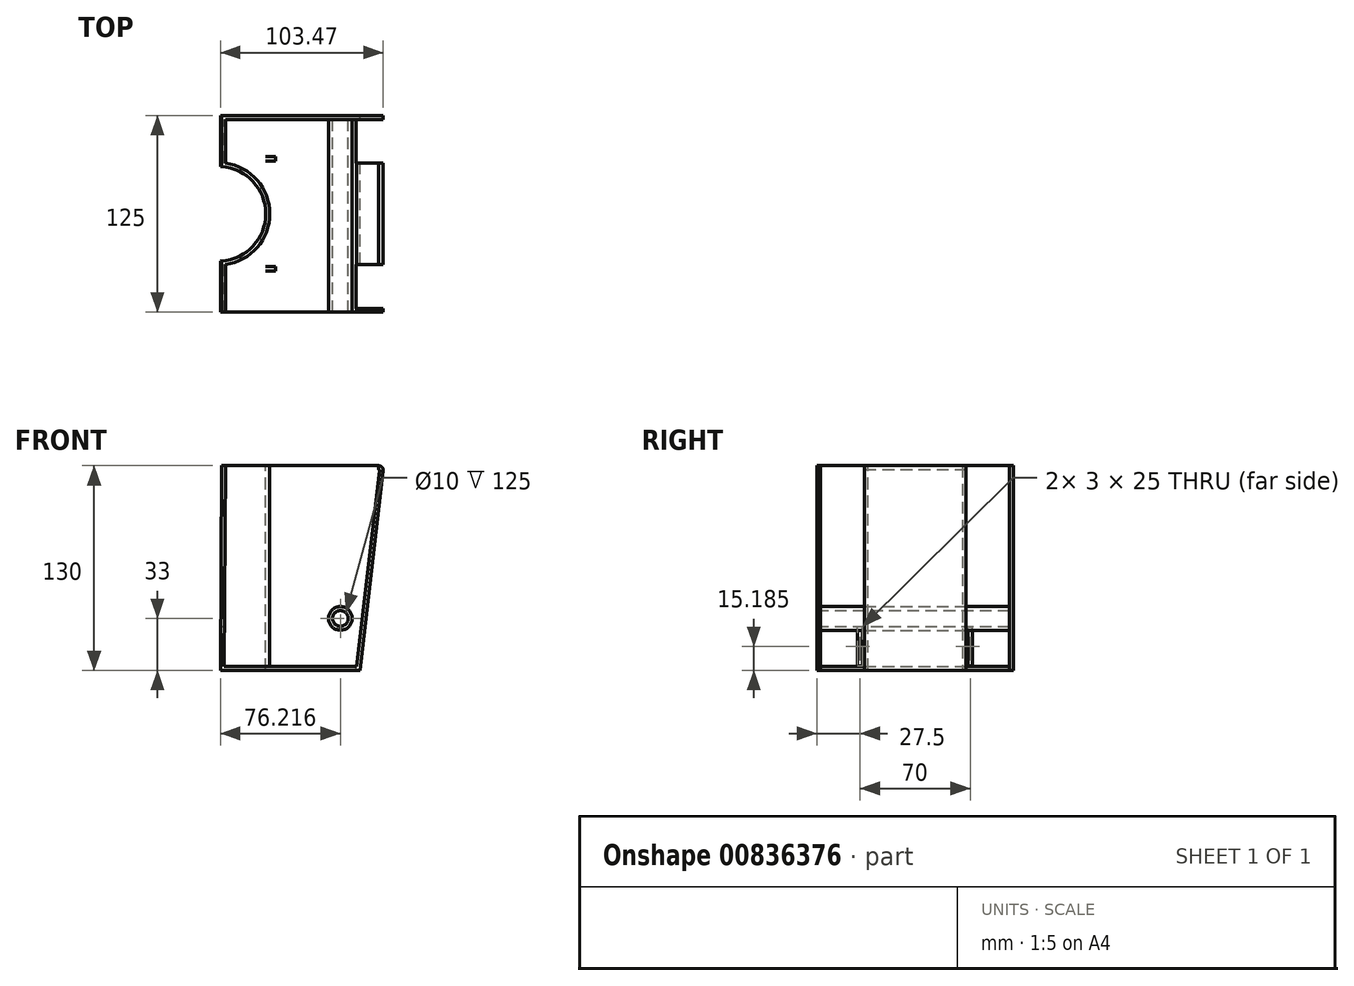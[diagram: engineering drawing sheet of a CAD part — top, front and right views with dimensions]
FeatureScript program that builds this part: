
annotation { "Feature Type Name" : "Feature", "Feature Type Description" : "" }
export const myFeature = defineFeature(function(context is Context, id is Id, definition is map)
    precondition{}
    {
        {
            var Q0;
            Q0=qCreatedBy(makeId("Front.planeOp"),FACE);
            var sketch = newSketch(context, id + "F0", { "sketchPlane" : qUnion([Q0])});
            skLineSegment(sketch, "E0", {"start": v(0, 130) * mm, "end": v(75, 130) * mm});
            skLineSegment(sketch, "E1", {"start": v(75, 130) * mm, "end": v(60, 0) * mm});
            skLineSegment(sketch, "E2", {"start": v(0, 130) * mm, "end": v(-28, 130) * mm});
            skLineSegment(sketch, "E3", {"start": v(-28.83, 0) * mm, "end": v(-28, 130) * mm});
            skLineSegment(sketch, "E4", {"start": v(75.45, 0) * mm, "end": v(-49.86, 0) * mm, "construction": true});
            skLineSegment(sketch, "E5", {"start": v(0, -37.66) * mm, "end": v(0, 158.2) * mm, "construction": true});
            skLineSegment(sketch, "E6", {"start": v(-28.83, 0) * mm, "end": v(60, 0) * mm});
            skPoint(sketch, "E7.start.orphan", {"position": v(0, -15) * mm});
            skLineSegment(sketch, "E8", {"start": v(-28.62, 33) * mm, "end": v(47.39, 33) * mm, "construction": true});
            skLineSegment(sketch, "E9", {"start": v(47.39, 0) * mm, "end": v(47.39, 50.91) * mm, "construction": true});
            skCircle(sketch, "E10", {"center": v(47.39, 33) * mm, "radius": 5 * mm});
            skSolve(sketch);
        }
        {
            var Q0;
            Q0=makeQuery(id+"F0.imprint","IMPRINT",FACE,{"disambiguationData":[TD([[makeQuery(id+"F0.imprint","IMPRINT",EDGE,{"derivedFrom":sQuery(id+"F0.wireOp",EDGE,"E0")}),-1.0]])]});
            var Q1;
            Q1=qSketchRegion(id+"F3",true);
            extrude(context, id + "F1", {"entities" : qUnion([Q0, Q1]), "depth" : 125 * mm, "offsetDistance" : 25 * mm});
        }
        {
            var Q0;
            Q0=makeQuery(id+"F1.opExtrude","SWEPT_FACE",FACE,{"disambiguationData":[OSD([sQuery(id+"F0.wireOp",EDGE,"E0"),sQuery(id+"F0.wireOp",EDGE,"E2")])]});
            cPlane(context, id + "F2", {"entities" : qUnion([Q0]), "cplaneType" : CPlaneType.OFFSET, "offset" : 0 * mm, "width" : 150 * mm, "height" : 150 * mm});
        }
        {
            var Q0;
            Q0=qCreatedBy(id+"F2.planeOp",FACE);
            var sketch = newSketch(context, id + "F3", { "sketchPlane" : qUnion([Q0])});
            skCircle(sketch, "E11", {"center": v(-30, -62.5) * mm, "radius": 30 * mm});
            skLineSegment(sketch, "E12", {"start": v(0, 0) * mm, "end": v(0, -125) * mm, "construction": true});
            skLineSegment(sketch, "E13", {"start": v(0, 0) * mm, "end": v(0, -62.5) * mm, "construction": true});
            skSolve(sketch);
        }
        {
            var Q0;
            Q0=makeQuery(id+"F3.imprint","IMPRINT",FACE,{"disambiguationData":[TD([[makeQuery(id+"F3.imprint","IMPRINT",EDGE,{"derivedFrom":sQuery(id+"F3.wireOp",EDGE,"E11")}),1.0]])]});
            extrude(context, id + "F4", {"entities" : qUnion([Q0]), "operationType" : NewBodyOperationType.REMOVE, "oppositeDirection" : true, "depth" : 171.8 * mm, "offsetDistance" : 25 * mm});
        }
        {
            var Q0;
            Q0=makeQuery(id+"F1.opExtrude","SWEPT_EDGE",EDGE,{"disambiguationData":[OSD([sQuery(id+"F0.wireOp",EDGE,"E0"),sQuery(id+"F0.wireOp",EDGE,"E1")])]});
            fillet(context, id + "F5", {"entities" : qUnion([Q0]), "radius" : 3 * mm, "tangentPropagation" : true, "allowEdgeOverflow" : false});
        }
        {
            var Q0;
            Q0=makeQuery(id+"F1.opExtrude","SWEPT_FACE",FACE,{"disambiguationData":[OSD([sQuery(id+"F0.wireOp",EDGE,"E0"),sQuery(id+"F0.wireOp",EDGE,"E2")])]});
            var Q1;
            Q1=makeQuery(id+"F1.opExtrude","CAP_FACE",FACE,{"disambiguationData":[OSD([sQuery(id+"F0.wireOp",EDGE,"E0"),sQuery(id+"F0.wireOp",EDGE,"y3vMRWIf-u3MA-5TxN-y6xK-OTS8Fqzy5Pt6"),sQuery(id+"F0.wireOp",EDGE,"xp1ytB3h-V9W0-7MQi-CCPZ-iRdVjfuMOfr9"),sQuery(id+"F0.wireOp",EDGE,"646e11d9-17b4-4f13-8456-ecb146ae1e03.trimOffspring"),sQuery(id+"F0.wireOp",EDGE,"E1"),sQuery(id+"F0.wireOp",EDGE,"E2"),sQuery(id+"F0.wireOp",EDGE,"E7"),sQuery(id+"F0.wireOp",EDGE,"E3")])],"isStart":false});
            shell(context, id + "F6", {"entities" : qUnion([Q0, Q1]), "thickness" : 2.5 * mm});
        }
        {
            var Q0;
            {var subQ0=sQuery(id+"F0.wireOp",EDGE,"E3");var subQ1=sQuery(id+"F0.wireOp",EDGE,"E7");var subQ2=sQuery(id+"F0.wireOp",EDGE,"E2");var subQ3=sQuery(id+"F0.wireOp",EDGE,"xp1ytB3h-V9W0-7MQi-CCPZ-iRdVjfuMOfr9");var subQ4=sQuery(id+"F0.wireOp",EDGE,"E0");Q0=makeQuery(id+"F4.boolean.opBoolean","SPLIT",FACE,{"disambiguationData":[TD([makeQuery(id+"F1.opExtrude","CAP_FACE",FACE,{"disambiguationData":[OSD([subQ4,sQuery(id+"F0.wireOp",EDGE,"y3vMRWIf-u3MA-5TxN-y6xK-OTS8Fqzy5Pt6"),subQ3,sQuery(id+"F0.wireOp",EDGE,"646e11d9-17b4-4f13-8456-ecb146ae1e03.trimOffspring"),sQuery(id+"F0.wireOp",EDGE,"E1"),subQ2,subQ1,subQ0])],"isStart":true})])],"derivedFrom":makeQuery(id+"F1.opExtrude","SWEPT_FACE",FACE,{"disambiguationData":[OSD([subQ0])]})});}
            cPlane(context, id + "F7", {"entities" : qUnion([Q0]), "cplaneType" : CPlaneType.OFFSET, "offset" : 0 * mm, "width" : 150 * mm, "height" : 150 * mm});
        }
        {
            var Q0;
            Q0=qCreatedBy(id+"F7.planeOp",FACE);
            var sketch = newSketch(context, id + "F8", { "sketchPlane" : qUnion([Q0])});
            skLineSegment(sketch, "E14.bottom", {"start": v(29, 2.5) * mm, "end": v(26, 2.5) * mm});
            skLineSegment(sketch, "E14.top", {"start": v(29, 27.5) * mm, "end": v(26, 27.5) * mm});
            skLineSegment(sketch, "E14.left", {"start": v(29, 2.5) * mm, "end": v(29, 27.5) * mm});
            skLineSegment(sketch, "E14.right", {"start": v(26, 2.5) * mm, "end": v(26, 27.5) * mm});
            skLineSegment(sketch, "E15.bottom", {"start": v(96, 2.5) * mm, "end": v(99, 2.5) * mm});
            skLineSegment(sketch, "E15.top", {"start": v(96, 27.5) * mm, "end": v(99, 27.5) * mm});
            skLineSegment(sketch, "E15.left", {"start": v(96, 2.5) * mm, "end": v(96, 27.5) * mm});
            skLineSegment(sketch, "E15.right", {"start": v(99, 2.5) * mm, "end": v(99, 27.5) * mm});
            skLineSegment(sketch, "E16.bottom", {"start": v(99, 2.5) * mm, "end": v(96, 2.5) * mm});
            skSolve(sketch);
        }
        {
            var Q0;
            Q0=makeQuery(id+"F8.imprint","IMPRINT",FACE,{"disambiguationData":[TD([[makeQuery(id+"F8.imprint","IMPRINT",EDGE,{"derivedFrom":sQuery(id+"F8.wireOp",EDGE,"E14.bottom")}),-1.0]])]});
            var Q1;
            Q1=makeQuery(id+"F8.imprint","IMPRINT",FACE,{"disambiguationData":[TD([[makeQuery(id+"F8.imprint","IMPRINT",EDGE,{"derivedFrom":sQuery(id+"F8.wireOp",EDGE,"E15.top")}),-1.0]])]});
            extrude(context, id + "F9", {"entities" : qUnion([Q0, Q1]), "operationType" : NewBodyOperationType.REMOVE, "oppositeDirection" : true, "depth" : 35.1 * mm, "offsetDistance" : 25 * mm});
        }
        {
            var Q0;
            Q0=qCreatedBy(id+"F7.planeOp",FACE);
            cPlane(context, id + "F10", {"entities" : qUnion([Q0]), "cplaneType" : CPlaneType.OFFSET, "offset" : 110 * mm, "oppositeDirection" : true, "width" : 150 * mm, "height" : 150 * mm});
        }
        {
            var Q0;
            Q0=qCreatedBy(id+"F10.planeOp",FACE);
            var sketch = newSketch(context, id + "F11", { "sketchPlane" : qUnion([Q0])});
            skLineSegment(sketch, "E17.bottom", {"start": v(122.5, -15) * mm, "end": v(94.75, -15) * mm});
            skLineSegment(sketch, "E17.top", {"start": v(122.5, 135) * mm, "end": v(94.75, 135) * mm});
            skLineSegment(sketch, "E17.left", {"start": v(122.5, -15) * mm, "end": v(122.5, 135) * mm});
            skLineSegment(sketch, "E17.right", {"start": v(94.75, -15) * mm, "end": v(94.75, 135) * mm});
            skLineSegment(sketch, "E18.bottom", {"start": v(30.25, -15) * mm, "end": v(2.5, -15) * mm});
            skLineSegment(sketch, "E18.top", {"start": v(30.25, 135) * mm, "end": v(2.5, 135) * mm});
            skLineSegment(sketch, "E18.left", {"start": v(30.25, -15) * mm, "end": v(30.25, 135) * mm});
            skLineSegment(sketch, "E18.right", {"start": v(2.5, -15) * mm, "end": v(2.5, 135) * mm});
            skSolve(sketch);
        }
        {
            var Q0;
            Q0=makeQuery(id+"F11.imprint","IMPRINT",FACE,{"disambiguationData":[TD([[makeQuery(id+"F11.imprint","IMPRINT",EDGE,{"derivedFrom":sQuery(id+"F11.wireOp",EDGE,"E17.bottom")}),-1.0]])]});
            var Q1;
            Q1=makeQuery(id+"F11.imprint","IMPRINT",FACE,{"disambiguationData":[TD([[makeQuery(id+"F11.imprint","IMPRINT",EDGE,{"derivedFrom":sQuery(id+"F11.wireOp",EDGE,"E18.bottom")}),-1.0]])]});
            extrude(context, id + "F12", {"entities" : qUnion([Q0, Q1]), "operationType" : NewBodyOperationType.REMOVE, "depth" : 23.73 * mm, "offsetDistance" : 25 * mm});
        }
    });
